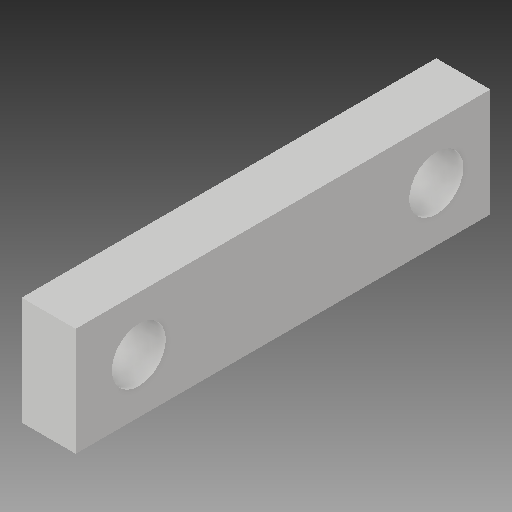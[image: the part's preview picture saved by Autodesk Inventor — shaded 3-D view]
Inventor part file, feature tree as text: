
AUTODESK INVENTOR PART (.ipt)
format: ipt  version: 2018 (Build 220112000, 112)  size: 102,400 bytes
history: native  units: in
note: dims shown in document units (in); Inventor stores cm internally (conversion verified against a paired STEP export)
features: reference x5, extrude x2, sketch x2, other x2
ambient origin geometry x8: Origin, YZ Plane, XZ Plane, XY Plane, X Axis, Y Axis, Z Axis, Center Point
bodies: Solid1 (feature_tree)
feature tree (11):
  extrude  "Extrusion1"  Depth=0.1181in
  extrude  "Extrusion2"  Depth=0.1181in
  sketch  "Sketch1"  dims[d0=0.315in d1=0.5906in d2=0.0in d3=0.0in d4=0.1181in]
  reference  "Reference1"
  reference  "Reference2"
  reference  "Reference3"
  reference  "Reference4"
  sketch  "Sketch2"  dims[d5=0.1181in d6=0.4724in d7=0.1772in d8=0.315in d9=0.0in]
  reference  "Reference5"
  other  "Bearing Support.iam"
  other  "Bearing risers:1"
